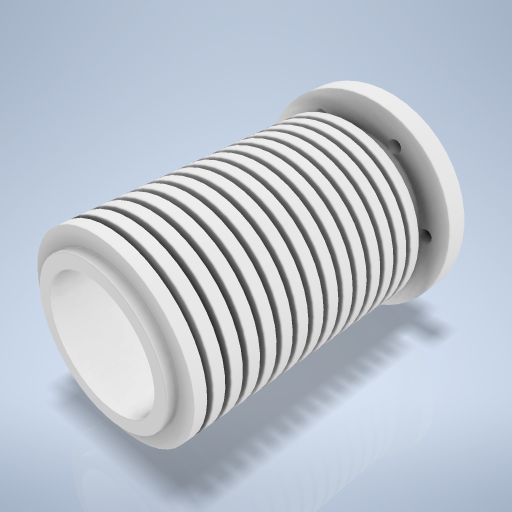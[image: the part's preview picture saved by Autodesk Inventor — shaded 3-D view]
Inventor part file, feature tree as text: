
AUTODESK INVENTOR PART (.ipt)
format: ipt  version: 2024.2 (Build 282272000, 272)  size: 473,600 bytes
history: native  units: mm
features: sketch x4, hole x2, extrude x1, plane x1, revolve x1, pattern_circular x1, projected_geometry x1
ambient origin geometry x8: Origin, YZ Plane, XZ Plane, XY Plane, X Axis, Y Axis, Z Axis, Center Point
bodies: Volumenkörper1 (feature_tree)
feature tree (11):
  extrude  "Extrusion1"  Depth=235.0mm TaperAngle=0.0deg
  plane  "Arbeitsebene1"
  revolve  "Umdrehung1"
  hole  "Bohrung1"  [1 undecoded]
  hole  "Bohrung2"  [1 undecoded]
  pattern_circular  "Runde Anordnung1"  Count=15  [1 undecoded]
  sketch  "Skizze1"  dims[d0=110.0mm d1=235.0mm d2=0.0mm]
  sketch  "Skizze2"  dims[d3=0.0mm d4=7.0mm]
  projected_geometry  "Projizierte Kontur1"
  sketch  "Skizze3"  dims[d5=8.5mm d6=135.0mm d7=150.0mm d9=12.5mm d10=10.0mm d12=10.0mm]
  sketch  "Skizze4"  dims[d14=360.0deg d15=16.0mm d16=11.0mm d17=155.0mm d18=90.0mm d19=6.0mm d20=95.0mm d21=10.0mm d22=90.0deg d23=8.0mm d24=20.594885mm d25=120.0mm d26=60.0deg d27=30.0deg d28=10.0mm d29=20.0mm d30=4.0mm d31=2.0mm d32=90.0deg d33=30.0mm d34=0.0mm d35=60.0mm d36=360.0deg]
note: 3 required parameter values undecoded (feature->parameter linkage not recoverable at this tier; creation-order binding heuristic only, values carry confidence <= 0.55)
